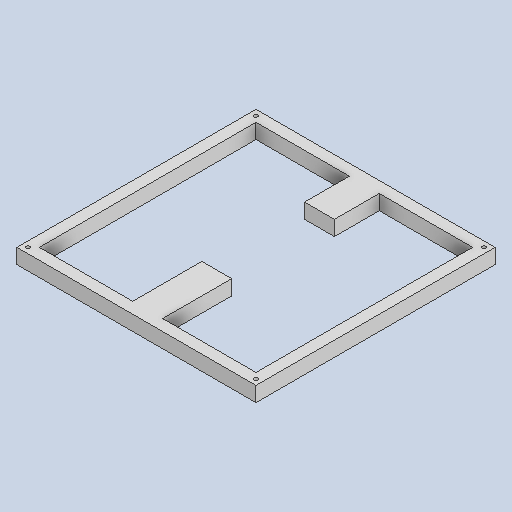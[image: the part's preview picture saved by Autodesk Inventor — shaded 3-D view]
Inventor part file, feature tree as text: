
AUTODESK INVENTOR PART (.ipt)
format: ipt  version: 2024 (Build 280153000, 153)  size: 294,912 bytes
history: native  units: in
note: dims shown in document units (in); Inventor stores cm internally (conversion verified against a paired STEP export)
features: extrude x2, projected_geometry x2
ambient origin geometry x8: Origin, YZ Plane, XZ Plane, XY Plane, X Axis, Y Axis, Z Axis, Center Point
bodies: Solid1 (feature_tree)
feature tree (4):
  extrude  "Extrusion1"  Depth=4.0in
  extrude  "Extrusion2"  Depth=4.0in
  projected_geometry  "Projected Loop1"
  projected_geometry  "Projected Loop2"
